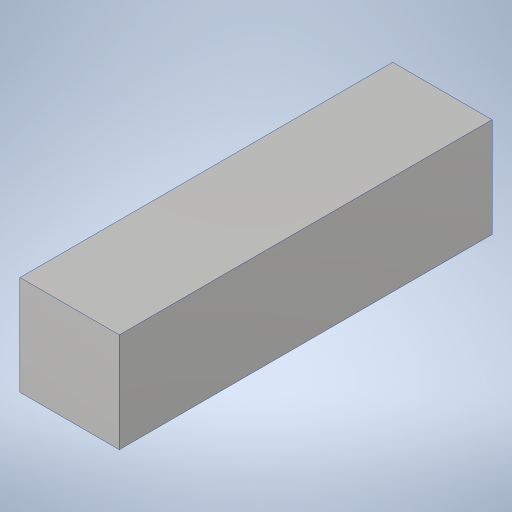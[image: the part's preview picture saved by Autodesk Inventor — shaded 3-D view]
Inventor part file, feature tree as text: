
AUTODESK INVENTOR PART (.ipt)
format: ipt  version: 2023.4 (Build 274418000, 418)  size: 186,880 bytes
history: native  units: in
note: dims shown in document units (in); Inventor stores cm internally (conversion verified against a paired STEP export)
features: extrude x1, sketch x1
ambient origin geometry x8: Origin, YZ Plane, XZ Plane, XY Plane, X Axis, Y Axis, Z Axis, Center Point
bodies: Solid1 (feature_tree)
feature tree (2):
  extrude  "Extrusion1"  Depth=4.0in
  sketch  "Sketch1"  dims[d0=4.0in d1=4.0in d2=15.0in d3=0.0in]
